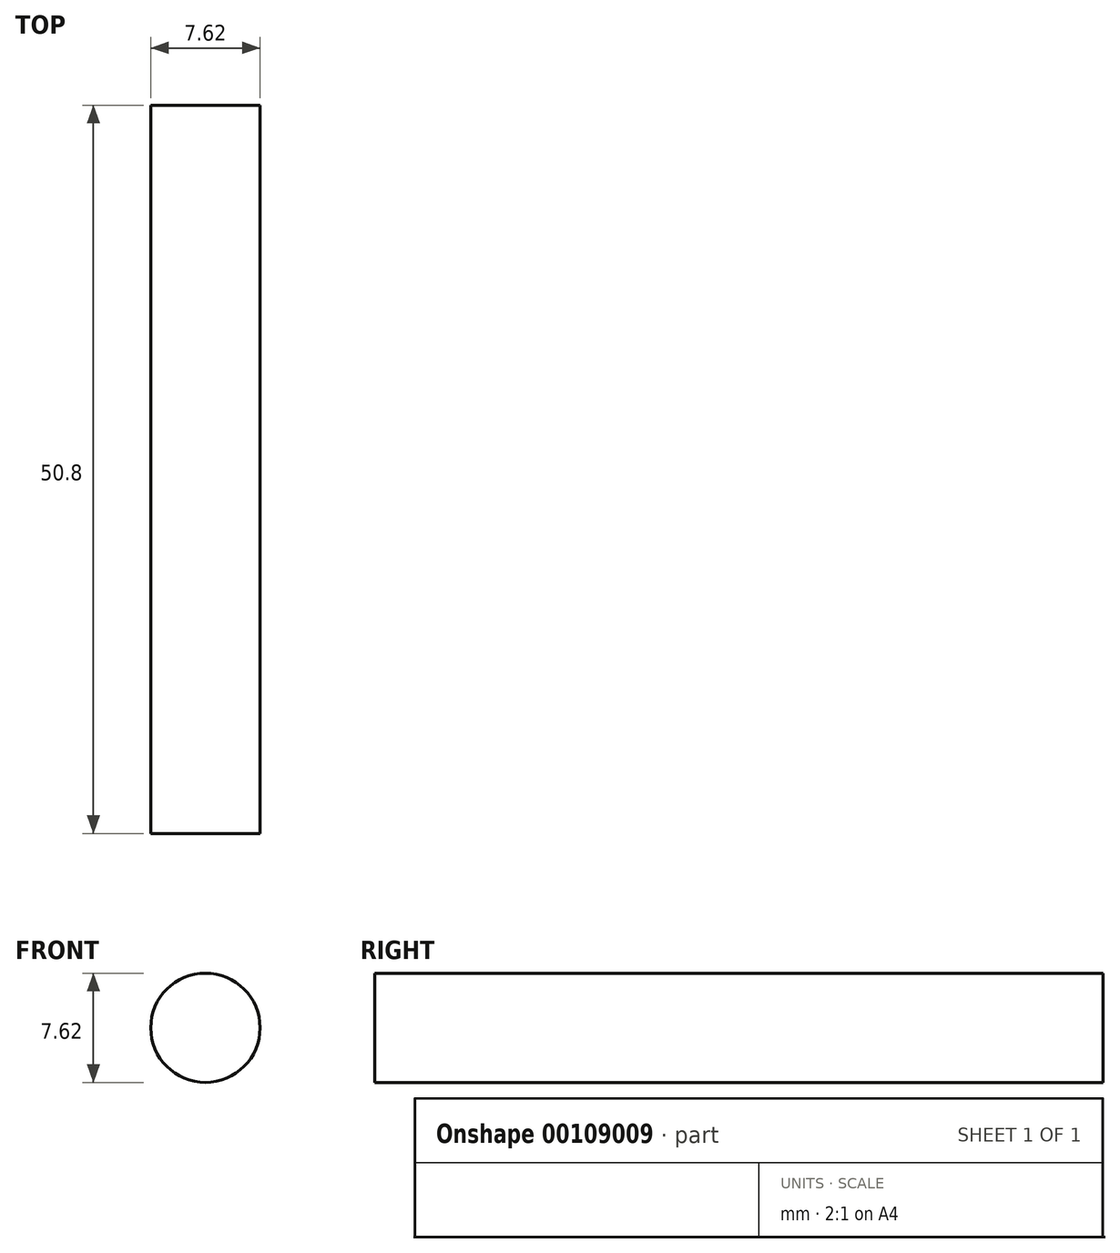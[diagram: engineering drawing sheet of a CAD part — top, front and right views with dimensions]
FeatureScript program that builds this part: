
annotation { "Feature Type Name" : "Feature", "Feature Type Description" : "" }
export const myFeature = defineFeature(function(context is Context, id is Id, definition is map)
    precondition{}
    {
        {
            var Q0;
            Q0=qCreatedBy(makeId("Front.planeOp"),FACE);
            var sketch = newSketch(context, id + "F0", { "sketchPlane" : qUnion([Q0])});
            skCircle(sketch, "E0", {"center": v(0, 0) * mm, "radius": 3.81 * mm});
            skSolve(sketch);
        }
        {
            var Q0;
            Q0=makeQuery(id+"F0.imprint","IMPRINT",FACE,{"disambiguationData":[TD([[makeQuery(id+"F0.imprint","IMPRINT",EDGE,{"derivedFrom":sQuery(id+"F0.wireOp",EDGE,"E0")}),1.0]])]});
            extrude(context, id + "F1", {"entities" : qUnion([Q0]), "depth" : 50.8 * mm});
        }
    });
